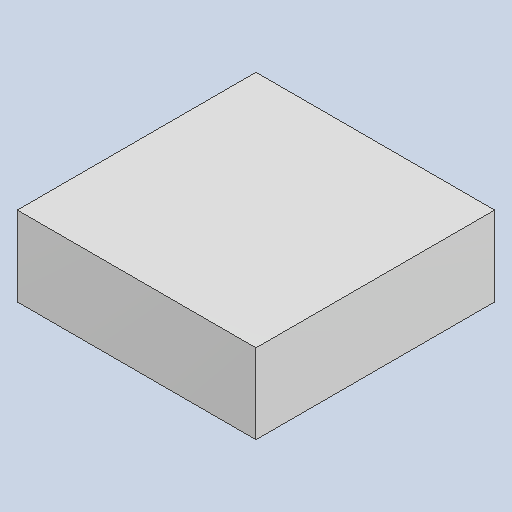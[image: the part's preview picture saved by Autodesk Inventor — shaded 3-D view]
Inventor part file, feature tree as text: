
AUTODESK INVENTOR PART (.ipt)
format: ipt  version: 2023.4 (Build 274418000, 418)  size: 79,872 bytes
history: native  units: mm
features: extrude x1
ambient origin geometry x8: Origin, YZ Plane, XZ Plane, XY Plane, X Axis, Y Axis, Z Axis, Center Point
bodies: Solid1 (feature_tree)
feature tree (1):
  extrude  "Extruded_46"  [1 undecoded]
note: 1 required parameter value undecoded (feature->parameter linkage not recoverable at this tier; creation-order binding heuristic only, values carry confidence <= 0.55)
